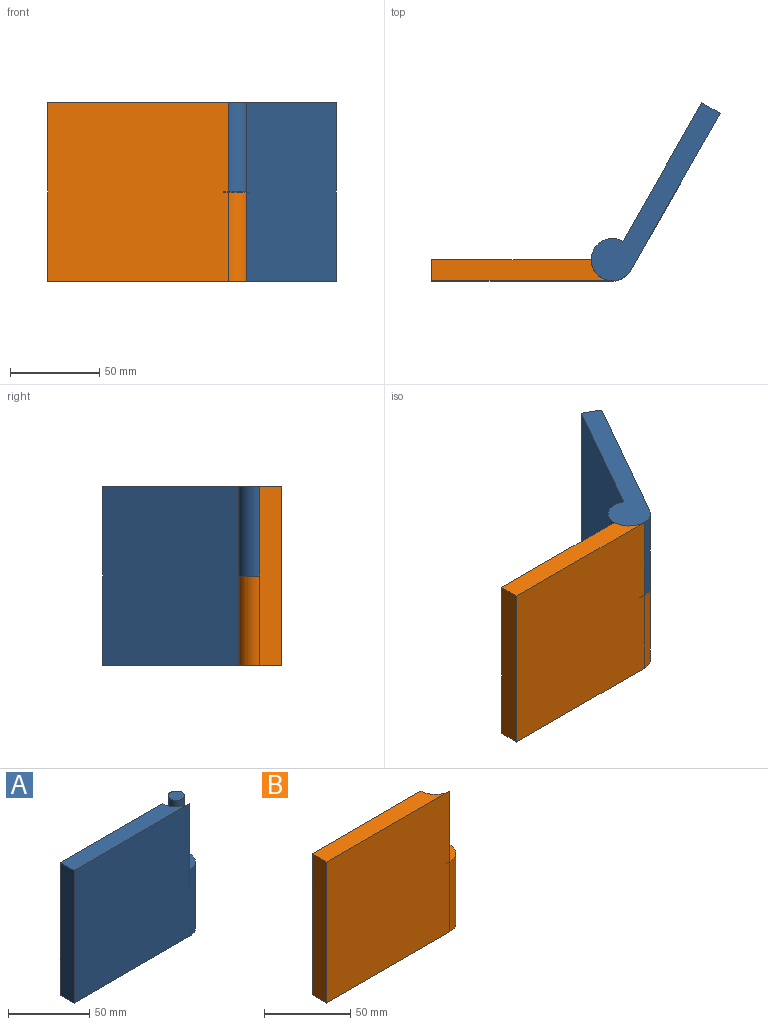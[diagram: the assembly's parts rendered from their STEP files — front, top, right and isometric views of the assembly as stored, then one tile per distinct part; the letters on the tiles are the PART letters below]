
ASSEMBLY  parts=2 mates=1
PART A: 10 faces, bbox 113x23.7x100 mm
  f0: cylinder r=11.87mm len=50mm, axis (0,0,-1), area 932.6mm2, adj f1,f3,f4,f7
  f1: plane 100x89.2mm, normal (0,1,0), area 8920.4mm2, adj f0,f2,f4,f5,f6
  f2: plane 100x11.87mm, normal (-1,0,0), area 1187.4mm2, adj f1,f3,f4,f5
  f3: plane 101.08x100mm, normal (0,-1,0), area 10107.8mm2, adj f0,f2,f4,f5,f6
  f4: plane 101.08x11.87mm, normal (0,0,1), area 1089.5mm2, adj f0,f1,f2,f3
  f5: plane 112.95x23.75mm, normal (0,0,-1), area 1532.4mm2, adj f1,f2,f3,f6
  f6: cylinder r=11.87mm len=50mm, axis (0,0,-1), area 2797.7mm2, adj f1,f3,f5,f7
  f7: plane 23.75x23.75mm, normal (0,0,1), area 364.4mm2, adj f0,f6,f9
  f8: plane 10x10mm, normal (0,0,1), area 78.5mm2, adj f9
  f9: cylinder r=5mm len=50mm, axis (0,0,-1), area 1570.8mm2, adj f7,f8
PART B: 9 faces, bbox 113x23.7x100 mm
  f0: cylinder r=11.87mm len=50mm, axis (0,0,-1), area 932.6mm2, adj f1,f3,f4,f8
  f1: plane 100x89.2mm, normal (0,1,0), area 8920.4mm2, adj f0,f2,f4,f5,f7
  f2: plane 100x11.87mm, normal (-1,0,0), area 1187.4mm2, adj f1,f3,f4,f5
  f3: plane 101.08x100mm, normal (0,-1,0), area 10107.8mm2, adj f0,f2,f4,f5,f7
  f4: plane 101.08x11.87mm, normal (0,0,1), area 1089.5mm2, adj f0,f1,f2,f3
  f5: plane 112.95x23.75mm, normal (0,0,-1), area 1453.9mm2, adj f1,f2,f3,f6,f7
  f6: cylinder r=5mm len=50mm, axis (0,0,-1), area 1570.8mm2, adj f5,f8
  f7: cylinder r=11.87mm len=50mm, axis (0,0,-1), area 2797.7mm2, adj f1,f3,f5,f8
  f8: plane 23.75x23.75mm, normal (0,0,1), area 364.4mm2, adj f0,f6,f7
PLACE A rot(axis=(0.5,-0.86,0),180deg) t=(39.5,20.33,111.35)mm
PLACE B t=(-31.2,-20.76,11.35)mm fixed
MATE revolute A.f0 <-> B.f0  axis (0,0,-1) through (12.64,-14.83,11.35)mm
